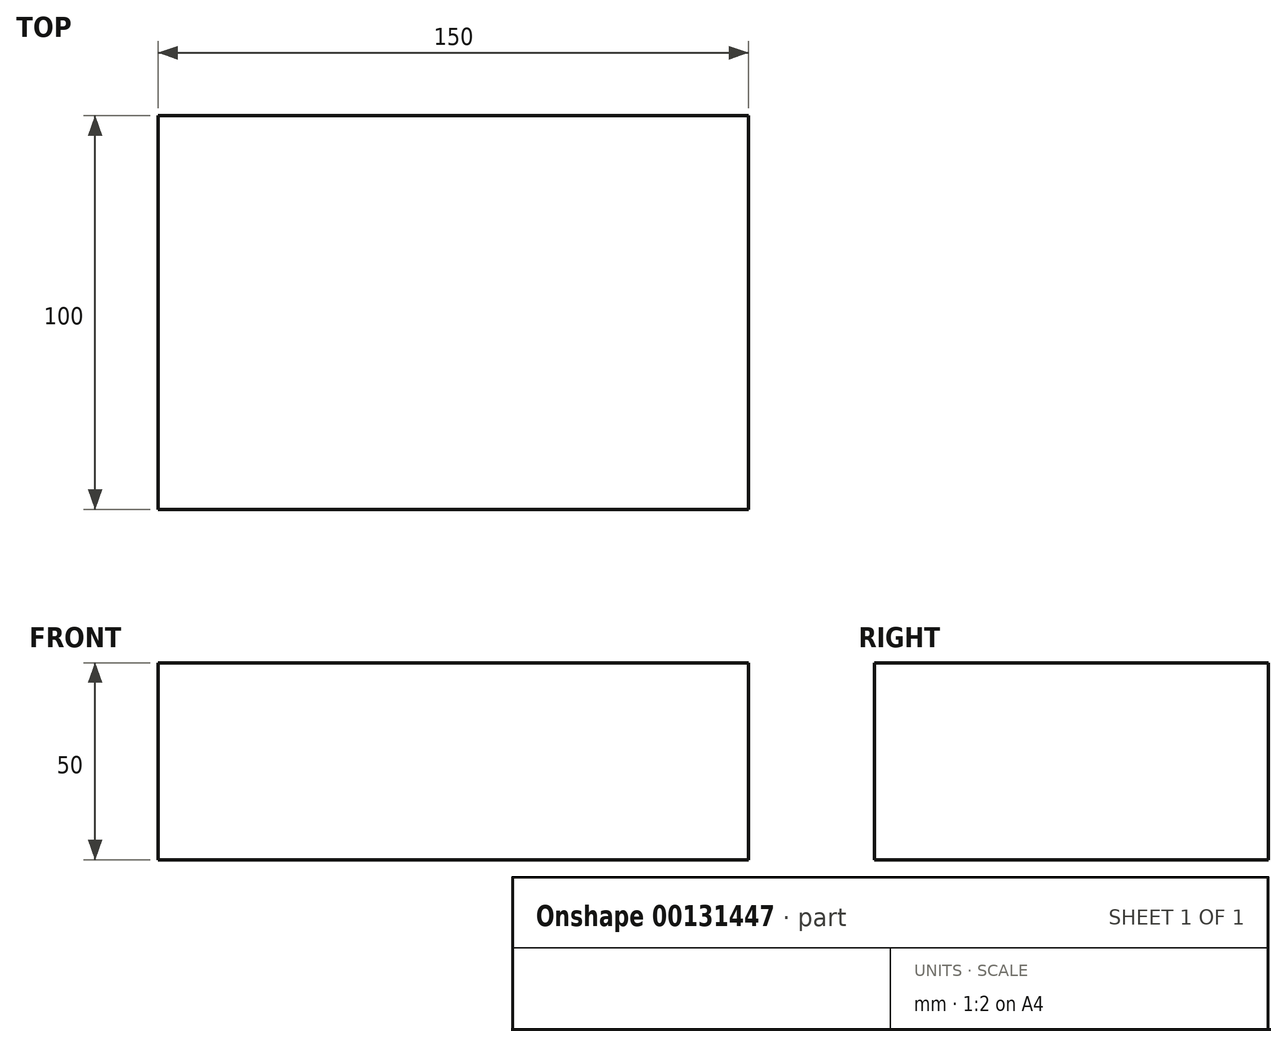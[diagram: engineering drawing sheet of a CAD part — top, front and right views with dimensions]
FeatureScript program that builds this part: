
annotation { "Feature Type Name" : "Feature", "Feature Type Description" : "" }
export const myFeature = defineFeature(function(context is Context, id is Id, definition is map)
    precondition{}
    {
        {
            var Q0;
            Q0=qCreatedBy(makeId("Top.planeOp"),FACE);
            var sketch = newSketch(context, id + "F0", { "sketchPlane" : qUnion([Q0])});
            skLineSegment(sketch, "E0.bottom", {"start": v(75, -50) * mm, "end": v(-75, -50) * mm});
            skLineSegment(sketch, "E0.top", {"start": v(75, 50) * mm, "end": v(-75, 50) * mm});
            skLineSegment(sketch, "E0.left", {"start": v(75, -50) * mm, "end": v(75, 50) * mm});
            skLineSegment(sketch, "E0.right", {"start": v(-75, -50) * mm, "end": v(-75, 50) * mm});
            skPoint(sketch, "E0.middle", {"position": v(0, 0) * mm});
            skSolve(sketch);
        }
        {
            var Q0;
            Q0 = qSketchRegion(id + "F0", true);
            var Q1;
            Q1=makeQuery(id+"F0.imprint","IMPRINT",FACE,{"disambiguationData":[TD([[makeQuery(id+"F0.imprint","IMPRINT",EDGE,{"derivedFrom":sQuery(id+"F0.wireOp",EDGE,"E0.bottom")}),-1.0]])]});
            extrude(context, id + "F1", {"entities" : qUnion([Q0, Q1]), "depth" : 50 * mm});
        }
    });
